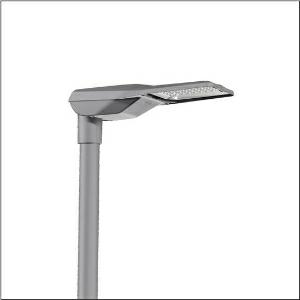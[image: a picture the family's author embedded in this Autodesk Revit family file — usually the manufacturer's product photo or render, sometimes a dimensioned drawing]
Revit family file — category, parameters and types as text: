
# Revit family: streetlight_sl_21_iq_mini___p0_8a_5xe2u31g08hb_4850
name_source: partatom
category: Lighting Fixtures
units: mm (PartAtom-declared; Revit-internal decimal feet)

## family parameters
Cut with Voids When Loaded = No
Host = Face
Light Source = No
Part Type = Normal
Room Calculation Point = No
Round Connector Dimension = Use Diameter
Shared = No

## types (1)
- --- (1 x LED, 9540 lm, 70.9 W, 3000K)
    Apparent Load = 71 VA
    CIE Flux Codes = 33 69 96 100 100
    Color Rendering = 70
    Color Temperature = 3000K
    Default Elevation = 1800 mm
    Description = Streetlight SL 21 iQ mini, mast luminaire, primary light control with lens, of PMMA, primary optical cover: cover, of toughened safety glass, transparent, light distribution: P0.8a, light emission: direct distribution, primary light characteristic: asymmetric, installation type: post-top, side-entry, LED, High Power LED, rated luminous flux: 9.540lm, luminous efficacy: 135lm/W, light colour: 730, colour temperature: 3000K, control gear: iQ Street-Remote, control: pre-setting: linear dimming characteristic, Street-Remote, Auto-Match, Temp-Guard, Lumen-Switch, Night-Set, Smart-Wire, Light-Fading, Desk-Remote (wireless, voltage-free reading and setting of iQ features in the workshop via application-optimized NFC function/RFID function), optimised constant luminous flux control (CLO 2.0), mains connection: 220..240V, AC, 50/60Hz, start of lifetime: 71W, end of service life: 75W, reduction: 31W, luminaire housing, of diecast aluminium, powder-coated, SITECO metallic grey (DB 702S), corrosivity category C5 high according to DIN EN ISO 12944, please order mast flange separately, inclination adjustable: 0°, 5°, 10°, 15°, sealing non-destructively replaceable, multi-level sealing system, length: 628mm, width: 235mm, height: 110mm, mast flange for spigot size: 42mm (side-entry): 5XC10008XM4, 60/48mm (side-entry/post-top): 5XC10108XM2, 76/60mm (side-entry/post-top): 5XC10108XM1, mounting height: 4..8m, protection rating (complete): IP66, insulation class (complete): insulation class II (safety insulation), certification: CE, ENEC, ENEC+, VDE, impact resistance: IK10, permissible operating ambient temperature for outdoor applications: -40..+50°C, standard-compliant lighting for roads and squares, packaging unit: 1 piece

Light Distribution: P0.8a
    Height = 110 mm
    Lamp = 1 x LED
    Lamp Light Flux = 9540 lm
    Lamp Power = 70.9 W
    Lamp count = 1
    Length = 625 mm
    Luminous efficacy = 135 lm/W
    Manufacturer = Siteco
    ModVariant = No
    Model = 5XE2U31G08HB
    Number of Poles = 1
    OnlyDefault = Yes
    Power Factor = 1
    Product Name = Streetlight SL 21 iQ mini | P0.8a
    Product group = mast luminaire | pylon top
    ProductGroupID = 6100
    Protection Class = Protection class II
    Protection Degree = IP 66
    RLX_Detail_Level = 1
    RLX_Emergency_Light_Flux = 0 lm
    RLX_Emergency_Type = 0
    RLX_Emergency_Type_DB = No
    RlxData = <blob elided: 92193 chars, md5=b6a0ff17>
    Socket = socket
    Standby Power = 0 W
    System Light Flux = 9540 lm
    System Power = 71 W
    Type Comments = factory setting: luminous flux: 100 % | dim-lin: 254 | 711 mA
    Type Image = l_1003519.jpg
    URL = http://relux.com
    VarID = @adj_080143
    Voltage = 0 V
    Weight = 0.00 kg
    Width = 234 mm

## geometry (parser evidence)
native form markers: Blend x4, Sweep x10
no freeform markers — native parametric forms only
